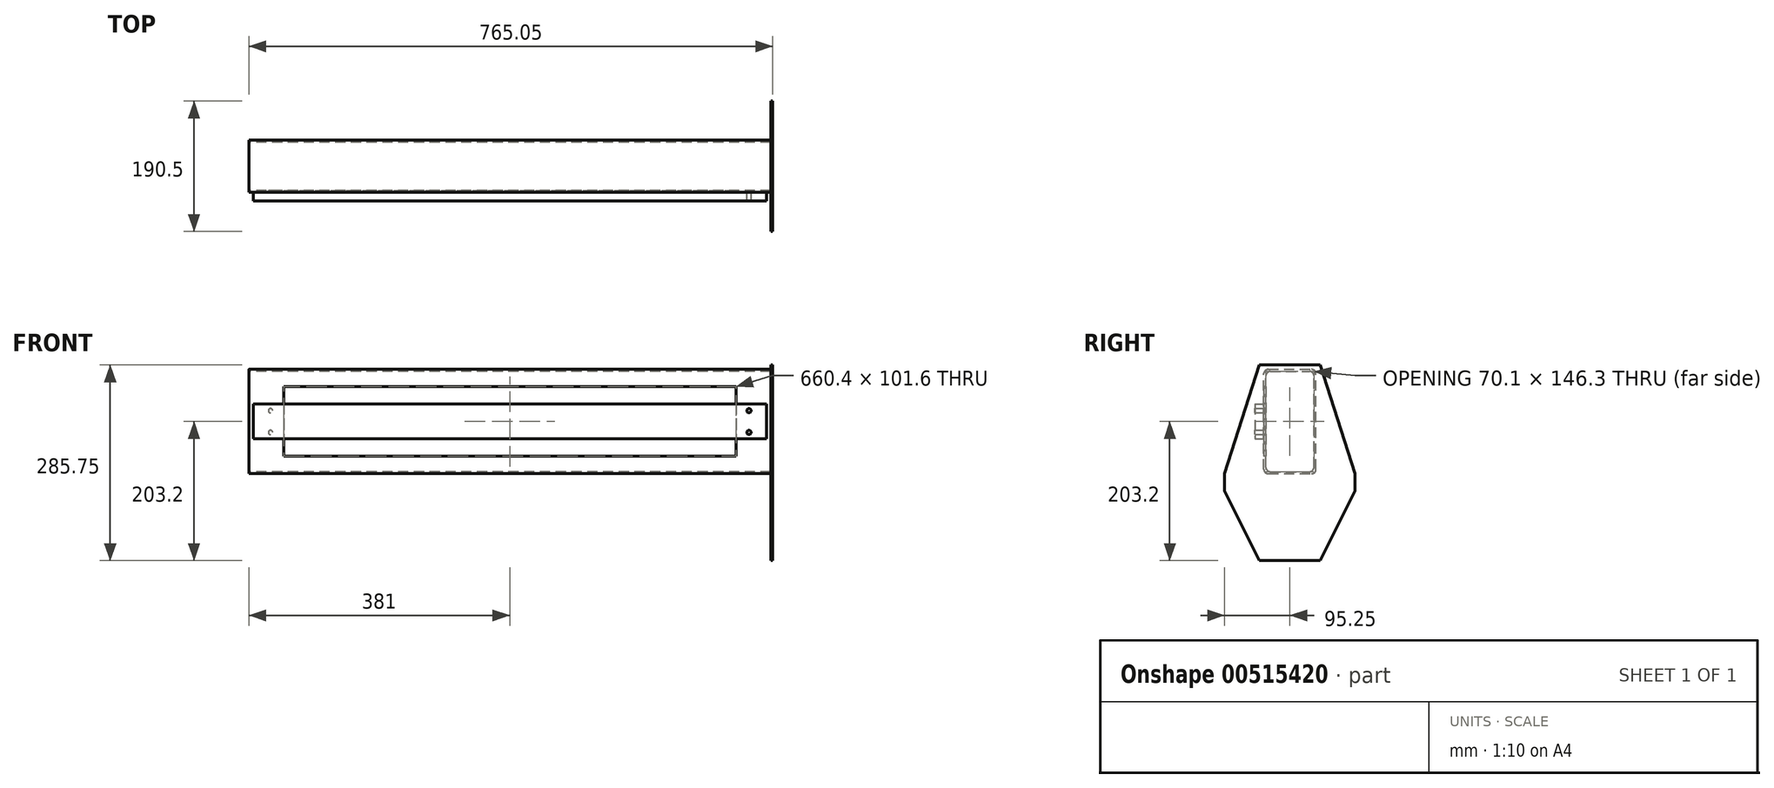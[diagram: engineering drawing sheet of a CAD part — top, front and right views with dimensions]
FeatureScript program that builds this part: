
annotation { "Feature Type Name" : "Feature", "Feature Type Description" : "" }
export const myFeature = defineFeature(function(context is Context, id is Id, definition is map)
    precondition{}
    {
        {
            var Q0;
            Q0=qCreatedBy(makeId("Right.planeOp"),FACE);
            var sketch = newSketch(context, id + "F0", { "sketchPlane" : qUnion([Q0])});
            skLineSegment(sketch, "E0.bottom", {"start": v(6.35, 0) * mm, "end": v(69.85, 0) * mm});
            skLineSegment(sketch, "E0.top", {"start": v(6.35, 152.4) * mm, "end": v(69.85, 152.4) * mm});
            skLineSegment(sketch, "E0.left", {"start": v(0, 6.35) * mm, "end": v(0, 146.05) * mm});
            skLineSegment(sketch, "E0.right", {"start": v(76.2, 6.35) * mm, "end": v(76.2, 146.05) * mm});
            skLineSegment(sketch, "E1.0", {"start": v(73.15, 9.4) * mm, "end": v(73.15, 143) * mm});
            skLineSegment(sketch, "E1.1", {"start": v(9.4, 3.05) * mm, "end": v(66.8, 3.05) * mm});
            skLineSegment(sketch, "E1.2", {"start": v(3.05, 9.4) * mm, "end": v(3.05, 143) * mm});
            skLineSegment(sketch, "E1.3", {"start": v(9.4, 149.35) * mm, "end": v(66.8, 149.35) * mm});
            skPoint(sketch, "E2.visualSharp", {"position": v(73.15, 149.35) * mm});
            skArc(sketch, "E2.filletArc", {"start": v(73.15, 143) * mm, "mid": v(71.3, 147.5) * mm, "end": v(66.8, 149.35) * mm});
            skPoint(sketch, "E3.visualSharp", {"position": v(73.15, 3.05) * mm});
            skArc(sketch, "E3.filletArc", {"start": v(66.8, 3.05) * mm, "mid": v(71.3, 4.9) * mm, "end": v(73.15, 9.4) * mm});
            skPoint(sketch, "E4.visualSharp", {"position": v(3.05, 3.05) * mm});
            skArc(sketch, "E4.filletArc", {"start": v(3.05, 9.4) * mm, "mid": v(4.9, 4.9) * mm, "end": v(9.4, 3.05) * mm});
            skPoint(sketch, "E5.visualSharp", {"position": v(3.05, 149.35) * mm});
            skArc(sketch, "E5.filletArc", {"start": v(9.4, 149.35) * mm, "mid": v(4.9, 147.5) * mm, "end": v(3.05, 143) * mm});
            skPoint(sketch, "E6.visualSharp", {"position": v(0, 152.4) * mm});
            skArc(sketch, "E6.filletArc", {"start": v(6.35, 152.4) * mm, "mid": v(1.86, 150.54) * mm, "end": v(0, 146.05) * mm});
            skPoint(sketch, "E7.visualSharp", {"position": v(76.2, 152.4) * mm});
            skArc(sketch, "E7.filletArc", {"start": v(76.2, 146.05) * mm, "mid": v(74.34, 150.54) * mm, "end": v(69.85, 152.4) * mm});
            skPoint(sketch, "E8.visualSharp", {"position": v(76.2, 0) * mm});
            skArc(sketch, "E8.filletArc", {"start": v(69.85, 0) * mm, "mid": v(74.34, 1.86) * mm, "end": v(76.2, 6.35) * mm});
            skPoint(sketch, "E9.visualSharp", {"position": v(0, 0) * mm});
            skArc(sketch, "E9.filletArc", {"start": v(0, 6.35) * mm, "mid": v(1.86, 1.86) * mm, "end": v(6.35, 0) * mm});
            skSolve(sketch);
        }
        {
            var Q0;
            Q0 = qSketchRegion(id + "F0", true);
            extrude(context, id + "F1", {"entities" : qUnion([Q0]), "depth" : 762 * mm, "offsetDistance" : 25.4 * mm});
        }
        {
            var Q0;
            Q0=makeQuery(id+"F1.opExtrude","SWEPT_FACE",FACE,{"disambiguationData":[OSD([sQuery(id+"F0.wireOp",EDGE,"E0.left")])]});
            var sketch = newSketch(context, id + "F2", { "sketchPlane" : qUnion([Q0])});
            skLineSegment(sketch, "E10.bottom", {"start": v(50.8, 127) * mm, "end": v(711.2, 127) * mm});
            skLineSegment(sketch, "E10.top", {"start": v(50.8, 25.4) * mm, "end": v(711.2, 25.4) * mm});
            skLineSegment(sketch, "E10.left", {"start": v(50.8, 127) * mm, "end": v(50.8, 25.4) * mm});
            skLineSegment(sketch, "E10.right", {"start": v(711.2, 127) * mm, "end": v(711.2, 25.4) * mm});
            skSolve(sketch);
        }
        {
            var Q0;
            Q0=makeQuery(id+"F2.imprint","IMPRINT",FACE,{"disambiguationData":[TD([[makeQuery(id+"F2.imprint","IMPRINT",EDGE,{"derivedFrom":sQuery(id+"F2.wireOp",EDGE,"E10.bottom")}),-1.0]])]});
            extrude(context, id + "F3", {"entities" : qUnion([Q0]), "operationType" : NewBodyOperationType.REMOVE, "oppositeDirection" : true, "depth" : 3.05 * mm, "offsetDistance" : 25.4 * mm});
        }
        {
            var Q0;
            Q0=makeQuery(id+"F1.opExtrude","SWEPT_FACE",FACE,{"disambiguationData":[OSD([sQuery(id+"F0.wireOp",EDGE,"E0.left")])]});
            var sketch = newSketch(context, id + "F4", { "sketchPlane" : qUnion([Q0])});
            skCircle(sketch, "E11", {"center": v(730.25, 92.07) * mm, "radius": 3.18 * mm});
            skCircle(sketch, "E12", {"center": v(730.25, 60.32) * mm, "radius": 3.17 * mm});
            skLineSegment(sketch, "E13", {"start": v(683.6, 76.2) * mm, "end": v(777, 76.2) * mm});
            skLineSegment(sketch, "E14", {"start": v(686.88, 101.6) * mm, "end": v(776.89, 101.6) * mm});
            skLineSegment(sketch, "E15", {"start": v(755.65, 162.14) * mm, "end": v(755.65, 16.53) * mm});
            skLineSegment(sketch, "E16", {"start": v(381, -161.33) * mm, "end": v(381, 577.37) * mm});
            skCircle(sketch, "E17.MirrorC", {"center": v(31.75, 60.32) * mm, "radius": 3.17 * mm});
            skCircle(sketch, "E18.MirrorC", {"center": v(31.75, 92.07) * mm, "radius": 3.18 * mm});
            skSolve(sketch);
        }
        {
            var Q0;
            Q0 = qSketchRegion(id + "F4", true);
            extrude(context, id + "F5", {"entities" : qUnion([Q0]), "operationType" : NewBodyOperationType.REMOVE, "oppositeDirection" : true, "depth" : 25.4 * mm, "offsetDistance" : 25.4 * mm});
        }
        {
            var Q0;
            Q0=makeQuery(id+"F1.opExtrude","SWEPT_FACE",FACE,{"disambiguationData":[OSD([sQuery(id+"F0.wireOp",EDGE,"E0.left")])]});
            var sketch = newSketch(context, id + "F6", { "sketchPlane" : qUnion([Q0])});
            skLineSegment(sketch, "E19.bottom", {"start": v(6.35, 101.6) * mm, "end": v(755.65, 101.6) * mm});
            skLineSegment(sketch, "E19.top", {"start": v(6.35, 50.8) * mm, "end": v(755.65, 50.8) * mm});
            skLineSegment(sketch, "E19.left", {"start": v(6.35, 101.6) * mm, "end": v(6.35, 50.8) * mm});
            skLineSegment(sketch, "E19.right", {"start": v(755.65, 101.6) * mm, "end": v(755.65, 50.8) * mm});
            skSolve(sketch);
        }
        {
            var Q0;
            Q0 = qSketchRegion(id + "F6", true);
            extrude(context, id + "F7", {"entities" : qUnion([Q0]), "depth" : 12.7 * mm, "offsetDistance" : 25.4 * mm});
        }
        {
            var Q0;
            Q0=makeQuery(id+"F1.opExtrude","SWEPT_FACE",FACE,{"disambiguationData":[OSD([sQuery(id+"F0.wireOp",EDGE,"E1.2")])]});
            var sketch = newSketch(context, id + "F8", { "sketchPlane" : qUnion([Q0])});
            skCircle(sketch, "E20", {"center": v(-730.25, 60.32) * mm, "radius": 3.18 * mm});
            skCircle(sketch, "E21", {"center": v(-730.25, 92.07) * mm, "radius": 3.17 * mm});
            skSolve(sketch);
        }
        {
            var Q0;
            Q0 = qSketchRegion(id + "F8", true);
            extrude(context, id + "F9", {"entities" : qUnion([Q0]), "operationType" : NewBodyOperationType.REMOVE, "endBound" : BoundingType.THROUGH_ALL, "oppositeDirection" : true, "depth" : 25.4 * mm, "offsetDistance" : 25.4 * mm});
        }
        {
            var Q0;
            Q0=makeQuery(id+"F1.opExtrude","CAP_FACE",FACE,{"disambiguationData":[OSD([sQuery(id+"F0.wireOp",EDGE,"E0.bottom"),sQuery(id+"F0.wireOp",EDGE,"E0.top"),sQuery(id+"F0.wireOp",EDGE,"E0.left"),sQuery(id+"F0.wireOp",EDGE,"E0.right"),sQuery(id+"F0.wireOp",EDGE,"E1.0"),sQuery(id+"F0.wireOp",EDGE,"E1.1"),sQuery(id+"F0.wireOp",EDGE,"E1.2"),sQuery(id+"F0.wireOp",EDGE,"E1.3"),sQuery(id+"F0.wireOp",EDGE,"E2.filletArc"),sQuery(id+"F0.wireOp",EDGE,"E3.filletArc"),sQuery(id+"F0.wireOp",EDGE,"E4.filletArc"),sQuery(id+"F0.wireOp",EDGE,"E5.filletArc"),sQuery(id+"F0.wireOp",EDGE,"E6.filletArc"),sQuery(id+"F0.wireOp",EDGE,"E7.filletArc"),sQuery(id+"F0.wireOp",EDGE,"E8.filletArc"),sQuery(id+"F0.wireOp",EDGE,"E9.filletArc")])],"isStart":false});
            var sketch = newSketch(context, id + "F10", { "sketchPlane" : qUnion([Q0])});
            skPoint(sketch, "E22.bottom.start.orphan", {"position": v(5.9, 152.4) * mm});
            skLineSegment(sketch, "E23.bottom", {"start": v(-6.35, 158.75) * mm, "end": v(82.55, 158.75) * mm});
            skLineSegment(sketch, "E23.top", {"start": v(-6.35, -127) * mm, "end": v(82.55, -127) * mm});
            skLineSegment(sketch, "E24", {"start": v(82.55, -127) * mm, "end": v(133.35, -25.4) * mm});
            skLineSegment(sketch, "E25", {"start": v(82.55, 158.75) * mm, "end": v(133.35, 0) * mm});
            skLineSegment(sketch, "E26", {"start": v(133.35, 0) * mm, "end": v(133.35, -25.4) * mm});
            skLineSegment(sketch, "E27", {"start": v(-57.15, 0) * mm, "end": v(-57.15, -25.4) * mm});
            skLineSegment(sketch, "E28", {"start": v(-57.15, -25.4) * mm, "end": v(-6.35, -127) * mm});
            skLineSegment(sketch, "E29", {"start": v(-6.35, 158.75) * mm, "end": v(-57.15, 0) * mm});
            skSolve(sketch);
        }
        {
            var Q0;
            Q0=makeQuery(id+"F10.imprint","IMPRINT",FACE,{"disambiguationData":[TD([[makeQuery(id+"F10.imprint","IMPRINT",EDGE,{"derivedFrom":makeQuery(id+"F1.opExtrude","CAP_EDGE",EDGE,{"disambiguationData":[OSD([sQuery(id+"F0.wireOp",EDGE,"E1.0")])],"isStart":false})}),1.0]])]});
            var Q1;
            Q1=makeQuery(id+"F10.imprint","IMPRINT",FACE,{"disambiguationData":[TD([[makeQuery(id+"F10.imprint","IMPRINT",EDGE,{"derivedFrom":makeQuery(id+"F1.opExtrude","CAP_EDGE",EDGE,{"disambiguationData":[OSD([sQuery(id+"F0.wireOp",EDGE,"E0.bottom")])],"isStart":false})}),1.0]])]});
            var Q2;
            Q2=makeQuery(id+"F10.imprint","IMPRINT",FACE,{"disambiguationData":[TD([[makeQuery(id+"F10.imprint","IMPRINT",EDGE,{"derivedFrom":sQuery(id+"F10.wireOp",EDGE,"E23.bottom")}),-1.0]])]});
            extrude(context, id + "F11", {"entities" : qUnion([Q0, Q1, Q2]), "depth" : 3.05 * mm, "offsetDistance" : 25.4 * mm});
        }
    });
